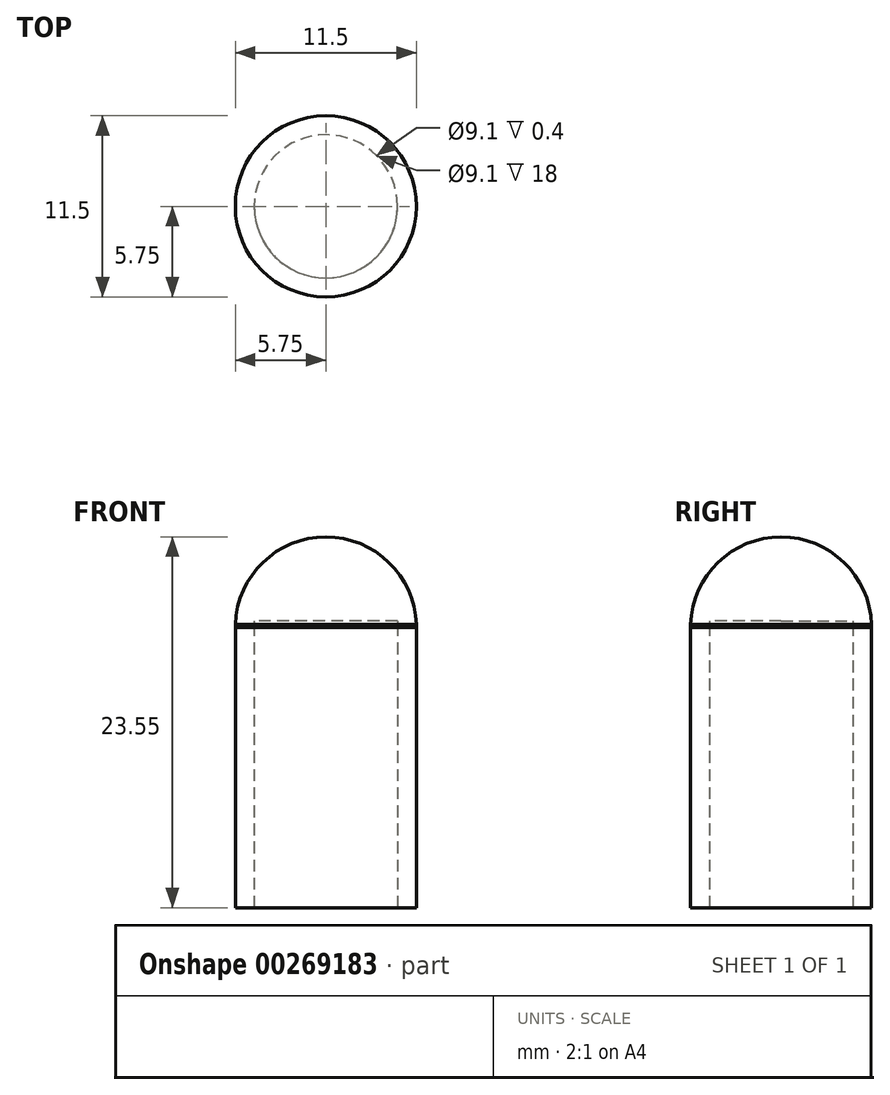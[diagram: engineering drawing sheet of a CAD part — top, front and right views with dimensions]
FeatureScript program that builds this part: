
annotation { "Feature Type Name" : "Feature", "Feature Type Description" : "" }
export const myFeature = defineFeature(function(context is Context, id is Id, definition is map)
    precondition{}
    {
        {
            var Q0;
            Q0=qCreatedBy(makeId("Top.planeOp"),FACE);
            var sketch = newSketch(context, id + "F0", { "sketchPlane" : qUnion([Q0])});
            skLineSegment(sketch, "E0", {"start": v(0, -5.75) * mm, "end": v(0, 5.75) * mm});
            skArc(sketch, "E1", {"start": v(0, 5.75) * mm, "mid": v(-5.75, 0) * mm, "end": v(0, -5.75) * mm});
            skArc(sketch, "E2", {"start": v(0, -5.75) * mm, "mid": v(5.75, 0) * mm, "end": v(0, 5.75) * mm});
            skSolve(sketch);
        }
        {
            var Q0;
            Q0=makeQuery(id+"F0.imprint","IMPRINT",FACE,{"disambiguationData":[TD([[makeQuery(id+"F0.imprint","IMPRINT",EDGE,{"derivedFrom":sQuery(id+"F0.wireOp",EDGE,"E1")}),1.0]])]});
            var Q1;
            Q1=makeQuery(id+"F0.imprint","IMPRINT",FACE,{"disambiguationData":[TD([[makeQuery(id+"F0.imprint","IMPRINT",EDGE,{"derivedFrom":sQuery(id+"F0.wireOp",EDGE,"E0")}),-1.0]])]});
            extrude(context, id + "F1", {"entities" : qUnion([Q0, Q1]), "depth" : 18 * mm});
        }
        {
            var Q0;
            Q0=makeQuery(id+"F0.imprint","IMPRINT",FACE,{"disambiguationData":[TD([[makeQuery(id+"F0.imprint","IMPRINT",EDGE,{"derivedFrom":sQuery(id+"F0.wireOp",EDGE,"E0")}),1.0]])]});
            var Q1;
            Q1=sQuery(id+"F0.wireOp",EDGE,"E0");
            revolve(context, id + "F2", {"entities" : qUnion([Q0]), "axis" : qUnion([Q1]), "revolveType" : RevolveType.ONE_DIRECTION, "angle" : 180 * degree});
        }
        {
            var Q0;
            Q0=makeQuery(id+"F2.opRevolve","SWEPT_BODY",BODY,{"disambiguationData":[OSD([sQuery(id+"F0.wireOp",EDGE,"E0"),sQuery(id+"F0.wireOp",EDGE,"E1")])]});
            var Q1;
            Q1=makeQuery(id+"F1.opExtrude","CAP_FACE",FACE,{"disambiguationData":[OSD([sQuery(id+"F0.wireOp",EDGE,"E1"),sQuery(id+"F0.wireOp",EDGE,"E2")])],"isStart":false});
            transform(context, id + "F3", {"entities" : qUnion([Q0]), "transformType" : TransformType.TRANSLATION_DISTANCE, "transformDirection" : qUnion([Q1]), "distance" : 17.8 * mm, "makeCopy" : false});
        }
        {
            var Q0;
            Q0=qCreatedBy(makeId("Top.planeOp"),FACE);
            var sketch = newSketch(context, id + "F4", { "sketchPlane" : qUnion([Q0])});
            skCircle(sketch, "E3", {"center": v(0, 0) * mm, "radius": 4.55 * mm});
            skSolve(sketch);
        }
        {
            var Q0;
            Q0=makeQuery(id+"F4.imprint","IMPRINT",FACE,{"disambiguationData":[TD([[makeQuery(id+"F4.imprint","IMPRINT",EDGE,{"derivedFrom":sQuery(id+"F4.wireOp",EDGE,"E3")}),1.0]])]});
            extrude(context, id + "F5", {"entities" : qUnion([Q0]), "operationType" : NewBodyOperationType.REMOVE, "depth" : 18.2 * mm});
        }
    });
